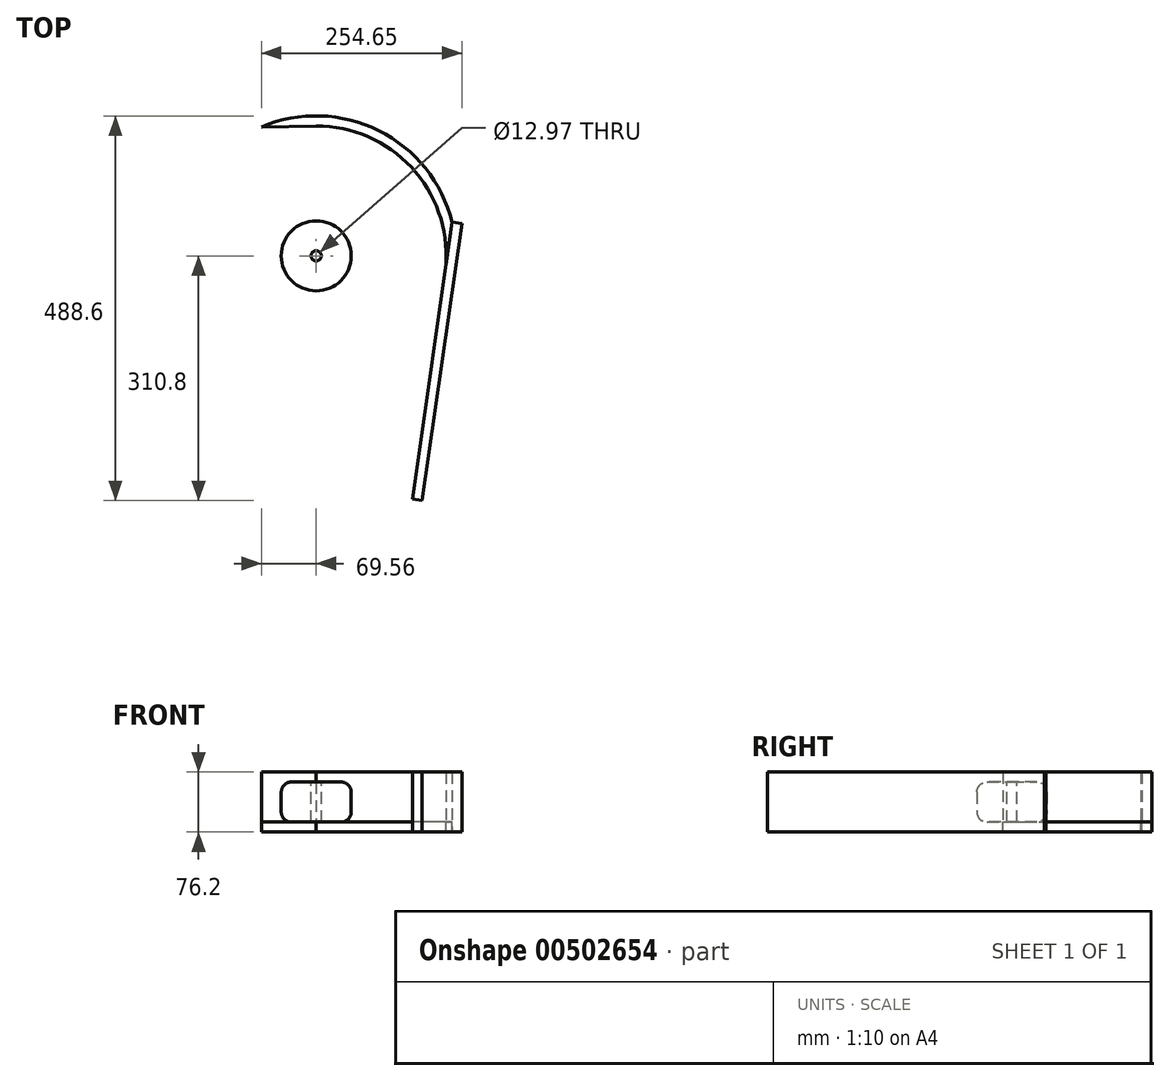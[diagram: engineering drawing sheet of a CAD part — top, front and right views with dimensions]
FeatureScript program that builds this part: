
annotation { "Feature Type Name" : "Feature", "Feature Type Description" : "" }
export const myFeature = defineFeature(function(context is Context, id is Id, definition is map)
    precondition{}
    {
        {
            var Q0;
            Q0=qCreatedBy(makeId("Top.planeOp"),FACE);
            var sketch = newSketch(context, id + "F0", { "sketchPlane" : qUnion([Q0])});
            skCircle(sketch, "E0", {"center": v(0, 0) * mm, "radius": 44.45 * mm});
            skSolve(sketch);
        }
        {
            var Q0;
            Q0=qSketchRegion(id+"F0",true);
            extrude(context, id + "F1", {"entities" : qUnion([Q0]), "depth" : 50.8 * mm});
        }
        {
            var Q0;
            Q0=makeQuery(id+"F1.opExtrude","SWEPT_FACE",FACE,{"disambiguationData":[OSD([sQuery(id+"F0.wireOp",EDGE,"E0")])]});
            var Q1;
            Q1=makeQuery(id+"F1.opExtrude","CAP_FACE",FACE,{"disambiguationData":[OSD([sQuery(id+"F0.wireOp",EDGE,"E0")])],"isStart":true});
            fillet(context, id + "F2", {"entities" : qUnion([Q0, Q1]), "radius" : 12.7 * mm, "tangentPropagation" : true, "allowEdgeOverflow" : false});
        }
        {
            var Q0;
            Q0=makeQuery(id+"F1.opExtrude","CAP_FACE",FACE,{"disambiguationData":[OSD([sQuery(id+"F0.wireOp",EDGE,"E0")])],"isStart":false});
            var sketch = newSketch(context, id + "F3", { "sketchPlane" : qUnion([Q0])});
            skCircle(sketch, "E1", {"center": v(0, 0) * mm, "radius": 6.48 * mm});
            skSolve(sketch);
        }
        {
            var Q0;
            Q0=makeQuery(id+"F3.imprint","IMPRINT",FACE,{"disambiguationData":[TD([[makeQuery(id+"F3.imprint","IMPRINT",EDGE,{"derivedFrom":sQuery(id+"F3.wireOp",EDGE,"E1")}),1.0]])]});
            extrude(context, id + "F4", {"entities" : qUnion([Q0]), "operationType" : NewBodyOperationType.REMOVE, "oppositeDirection" : true, "depth" : 76.2 * mm});
        }
        {
            var Q0;
            Q0=qCreatedBy(makeId("Top.planeOp"),FACE);
            var sketch = newSketch(context, id + "F5", { "sketchPlane" : qUnion([Q0])});
            skArc(sketch, "E2", {"start": v(164.7, -11.55) * mm, "mid": v(120.76, 112.58) * mm, "end": v(0, 165.1) * mm});
            skPoint(sketch, "E3", {"position": v(-165.1, 0) * mm});
            skPoint(sketch, "E4", {"position": v(122.63, -110.55) * mm});
            skPoint(sketch, "E5", {"position": v(0, 165.1) * mm});
            skArc(sketch, "E6", {"start": v(172.52, 43) * mm, "mid": v(79.3, 159.14) * mm, "end": v(-69.56, 163.63) * mm});
            skPoint(sketch, "E7", {"position": v(-69.56, 163.63) * mm});
            skPoint(sketch, "E8", {"position": v(130.11, -121.18) * mm});
            skLineSegment(sketch, "E9", {"start": v(-69.56, 163.63) * mm, "end": v(0, 165.1) * mm});
            skLineSegment(sketch, "E10", {"start": v(164.7, -11.55) * mm, "end": v(172.52, 43) * mm});
            skSolve(sketch);
        }
        {
            var Q0;
            Q0=makeQuery(id+"F5.imprint","IMPRINT",FACE,{"disambiguationData":[TD([[makeQuery(id+"F5.imprint","IMPRINT",EDGE,{"derivedFrom":sQuery(id+"F5.wireOp",EDGE,"E2")}),-1.0]])]});
            extrude(context, id + "F6", {"entities" : qUnion([Q0]), "depth" : 63.5 * mm});
        }
        {
            var Q0;
            Q0=makeQuery(id+"F6.opExtrude","CAP_FACE",FACE,{"disambiguationData":[OSD([sQuery(id+"F5.wireOp",EDGE,"E2"),sQuery(id+"F5.wireOp",EDGE,"E6"),sQuery(id+"F5.wireOp",EDGE,"hQ2aArEA-VtdC-3eQe-8VVH-7EDzHGcx1tkS"),sQuery(id+"F5.wireOp",EDGE,"E9")])],"isStart":true});
            extrude(context, id + "F7", {"entities" : qUnion([Q0]), "depth" : 12.7 * mm});
        }
        {
            var Q0;
            Q0=makeQuery(id+"F6.opExtrude","SWEPT_FACE",FACE,{"disambiguationData":[OSD([sQuery(id+"F5.wireOp",EDGE,"E10")])]});
            var sketch = newSketch(context, id + "F8", { "sketchPlane" : qUnion([Q0])});
            skLineSegment(sketch, "E11.bottom", {"start": v(-288.54, -12.7) * mm, "end": v(67.06, -12.7) * mm});
            skLineSegment(sketch, "E11.top", {"start": v(-288.54, 63.5) * mm, "end": v(67.06, 63.5) * mm});
            skLineSegment(sketch, "E11.left", {"start": v(-288.54, -12.7) * mm, "end": v(-288.54, 63.5) * mm});
            skLineSegment(sketch, "E11.right", {"start": v(67.06, -12.7) * mm, "end": v(67.06, 63.5) * mm});
            skSolve(sketch);
        }
        {
            var Q0;
            {var subQ1=sQuery(id+"F5.wireOp",EDGE,"E10");var subQ5=makeQuery(id+"F6.opExtrude","CAP_EDGE",EDGE,{"disambiguationData":[OSD([subQ1])],"isStart":true});Q0=makeQuery(id+"F8.imprint","IMPRINT",FACE,{"disambiguationData":[TD([[makeQuery(id+"F8.imprint","IMPRINT",EDGE,{"derivedFrom":subQ5}),1.0]])]});}
            var Q1;
            {var subQ3=sQuery(id+"F8.wireOp",EDGE,"E11.bottom");Q1=makeQuery(id+"F8.imprint","IMPRINT",FACE,{"disambiguationData":[TD([[makeQuery(id+"F8.imprint","IMPRINT",EDGE,{"derivedFrom":subQ3}),1.0]])]});}
            extrude(context, id + "F9", {"entities" : qUnion([Q0, Q1]), "depth" : 12.7 * mm});
        }
    });
